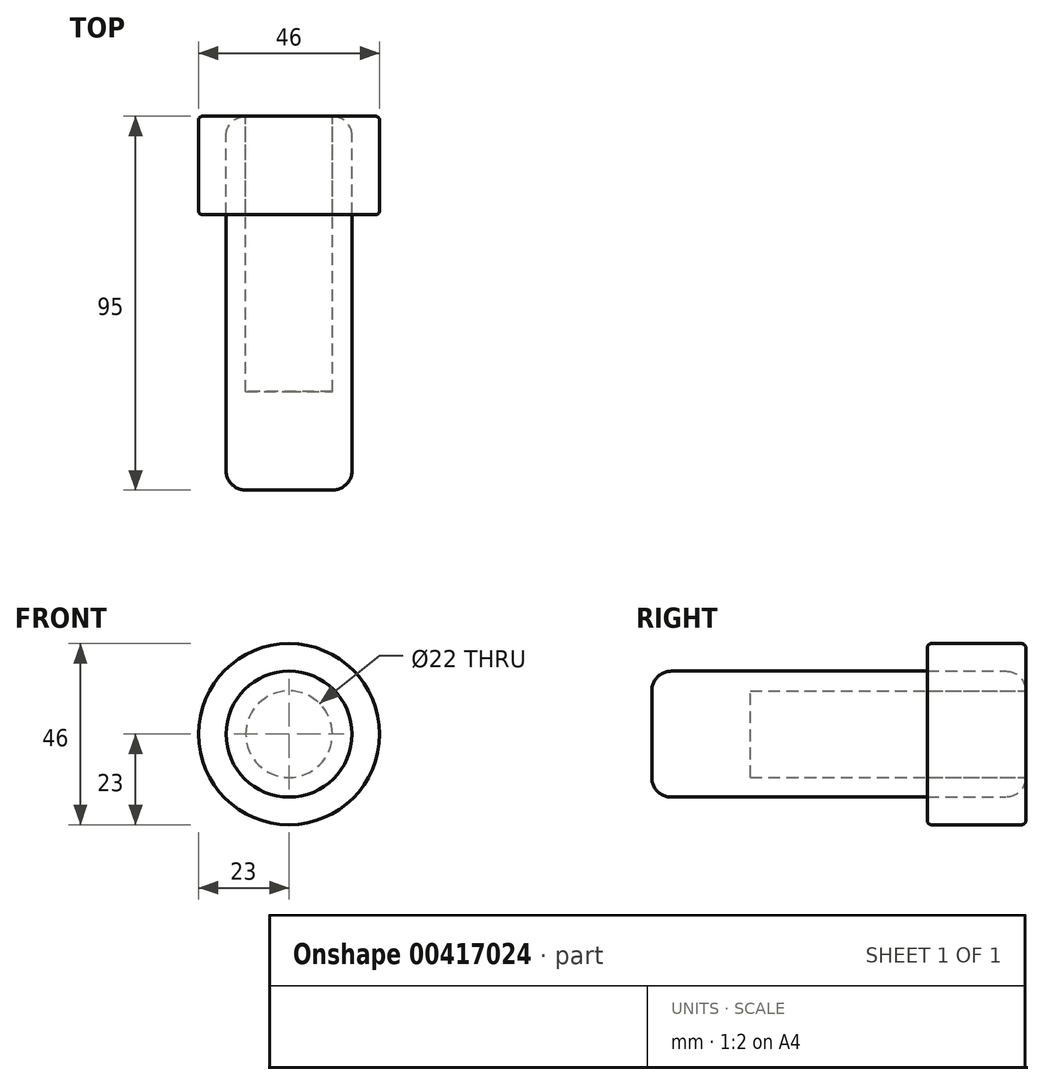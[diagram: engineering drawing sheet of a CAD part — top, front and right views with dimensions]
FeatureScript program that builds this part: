
annotation { "Feature Type Name" : "Feature", "Feature Type Description" : "" }
export const myFeature = defineFeature(function(context is Context, id is Id, definition is map)
    precondition{}
    {
        {
            var Q0;
            Q0=qCreatedBy(makeId("Front.planeOp"),FACE);
            var sketch = newSketch(context, id + "F0", { "sketchPlane" : qUnion([Q0])});
            skPoint(sketch, "E0.middle", {"position": v(0, 0) * mm});
            skCircle(sketch, "E1", {"center": v(0, 0) * mm, "radius": 23 * mm});
            skCircle(sketch, "E2", {"center": v(0, 0) * mm, "radius": 11 * mm});
            skCircle(sketch, "E3", {"center": v(0, 0) * mm, "radius": 16 * mm});
            skSolve(sketch);
        }
        {
            var Q0;
            Q0=makeQuery(id+"F0.imprint","IMPRINT",FACE,{"disambiguationData":[TD([[makeQuery(id+"F0.imprint","IMPRINT",EDGE,{"derivedFrom":sQuery(id+"F0.wireOp",EDGE,"E1")}),1.0]])]});
            var Q1;
            Q1=makeQuery(id+"F0.imprint","IMPRINT",FACE,{"disambiguationData":[TD([[makeQuery(id+"F0.imprint","IMPRINT",EDGE,{"derivedFrom":sQuery(id+"F0.wireOp",EDGE,"E2")}),-1.0]])]});
            extrude(context, id + "F1", {"entities" : qUnion([Q0, Q1]), "depth" : 25 * mm});
        }
        {
            var Q0;
            Q0=makeQuery(id+"F0.imprint","IMPRINT",FACE,{"disambiguationData":[TD([[makeQuery(id+"F0.imprint","IMPRINT",EDGE,{"derivedFrom":sQuery(id+"F0.wireOp",EDGE,"E2")}),1.0]])]});
            var Q1;
            Q1=makeQuery(id+"F0.imprint","IMPRINT",FACE,{"disambiguationData":[TD([[makeQuery(id+"F0.imprint","IMPRINT",EDGE,{"derivedFrom":sQuery(id+"F0.wireOp",EDGE,"E2")}),-1.0]])]});
            var Q2;
            Q2=sQuery(id+"F0.wireOp",EDGE,"E2");
            extrude(context, id + "F2", {"entities" : qUnion([Q0, Q1]), "surfaceEntities" : qUnion([Q2]), "depth" : 95 * mm});
        }
        {
            var Q0;
            Q0=makeQuery(id+"F0.imprint","IMPRINT",FACE,{"disambiguationData":[TD([[makeQuery(id+"F0.imprint","IMPRINT",EDGE,{"derivedFrom":sQuery(id+"F0.wireOp",EDGE,"E2")}),1.0]])]});
            extrude(context, id + "F3", {"entities" : qUnion([Q0]), "depth" : 70 * mm, "hasSecondDirection" : true, "secondDirectionOppositeDirection" : true, "secondDirectionDepth" : 0 * mm});
        }
        {
            var Q0;
            Q0=makeQuery(id+"F2.opExtrude","SWEPT_FACE",FACE,{"disambiguationData":[OSD([sQuery(id+"F0.wireOp",EDGE,"E3")])]});
            fillet(context, id + "F4", {"entities" : qUnion([Q0]), "radius" : 5 * mm, "tangentPropagation" : true, "allowEdgeOverflow" : false});
        }
        {
            var Q0;
            Q0=makeQuery(id+"F1.opExtrude","SWEPT_FACE",FACE,{"disambiguationData":[OSD([sQuery(id+"F0.wireOp",EDGE,"E1")])]});
            var Q1;
            Q1=makeQuery(id+"F1.opExtrude","CAP_EDGE",EDGE,{"disambiguationData":[OSD([sQuery(id+"F0.wireOp",EDGE,"E1")])],"isStart":true});
            var Q2;
            {var subQ0=sQuery(id+"F0.wireOp",EDGE,"E3");Q2=makeQuery(id+"F4.opFillet","BLEND_EDGE",EDGE,{"blendedFrom":[makeQuery(id+"F2.opExtrude","CAP_EDGE",EDGE,{"disambiguationData":[OSD([subQ0])],"isStart":true}),makeQuery(id+"F2.opExtrude","SWEPT_FACE",FACE,{"disambiguationData":[OSD([subQ0])]})],"blendedInto":[makeQuery(id+"F2.opExtrude","SWEPT_FACE",FACE,{"disambiguationData":[OSD([subQ0])]})]});}
            fillet(context, id + "F5", {"entities" : qUnion([Q0, Q1, Q2]), "radius" : 1 * mm, "tangentPropagation" : true, "allowEdgeOverflow" : false});
        }
    });
